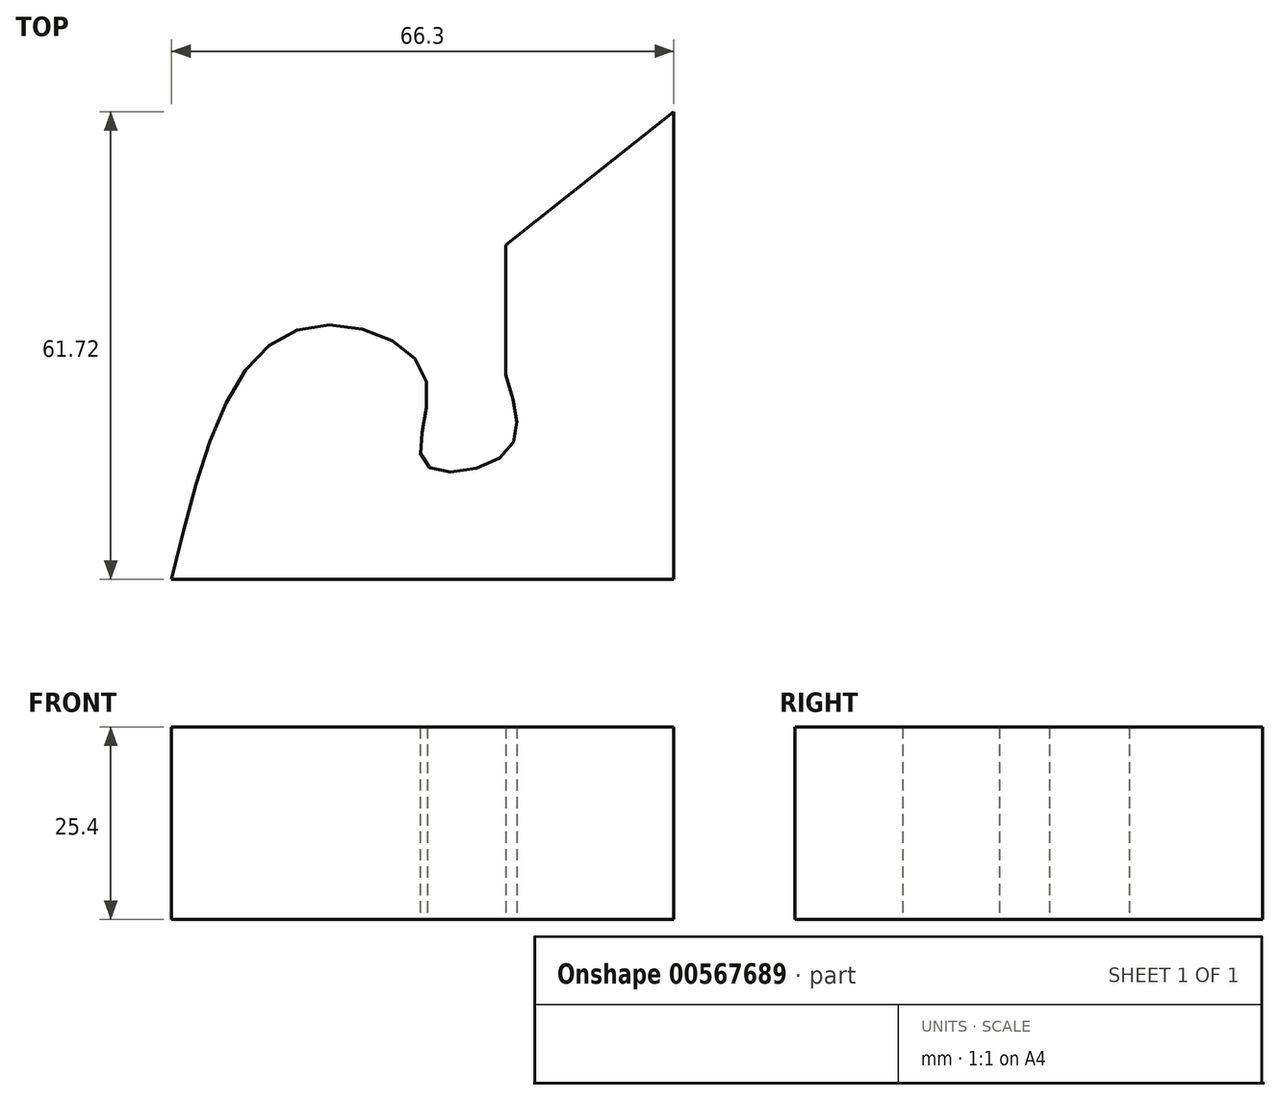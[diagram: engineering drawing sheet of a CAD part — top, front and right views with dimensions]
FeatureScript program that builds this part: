
annotation { "Feature Type Name" : "Feature", "Feature Type Description" : "" }
export const myFeature = defineFeature(function(context is Context, id is Id, definition is map)
    precondition{}
    {
        {
            var Q0;
            Q0=qCreatedBy(makeId("Top.planeOp"),FACE);
            var sketch = newSketch(context, id + "F0", { "sketchPlane" : qUnion([Q0])});
            skLineSegment(sketch, "E0", {"start": v(-33.38, -50.3) * mm, "end": v(32.92, -50.3) * mm});
            skLineSegment(sketch, "E1", {"start": v(32.92, -50.3) * mm, "end": v(32.92, 11.43) * mm});
            skLineSegment(sketch, "E2", {"start": v(32.92, 11.43) * mm, "end": v(10.74, -6.17) * mm});
            skFitSpline(sketch, "E3", {"points": [v(10.74, -6.17) * mm, v(10.74, -23.32) * mm, v(10.74, -24) * mm], "startDerivative": vector(0, -27.43) * mm, "endDerivative": vector(0, -2.74) * mm});
            skFitSpline(sketch, "E4", {"points": [v(10.74, -23.32) * mm, v(10.74, -33.6) * mm, v(0, -34.98) * mm, v(0, -23.32) * mm, v(-17.37, -17.6) * mm, v(-33.38, -50.3) * mm], "startDerivative": vector(23.43, -74.2) * mm, "endDerivative": vector(-35.1, -146.7) * mm});
            skSolve(sketch);
        }
        {
            var Q0;
            Q0 = qSketchRegion(id + "F0", true);
            extrude(context, id + "F1", {"entities" : qUnion([Q0]), "depth" : 25.4 * mm, "offsetDistance" : 25.4 * mm});
        }
    });
